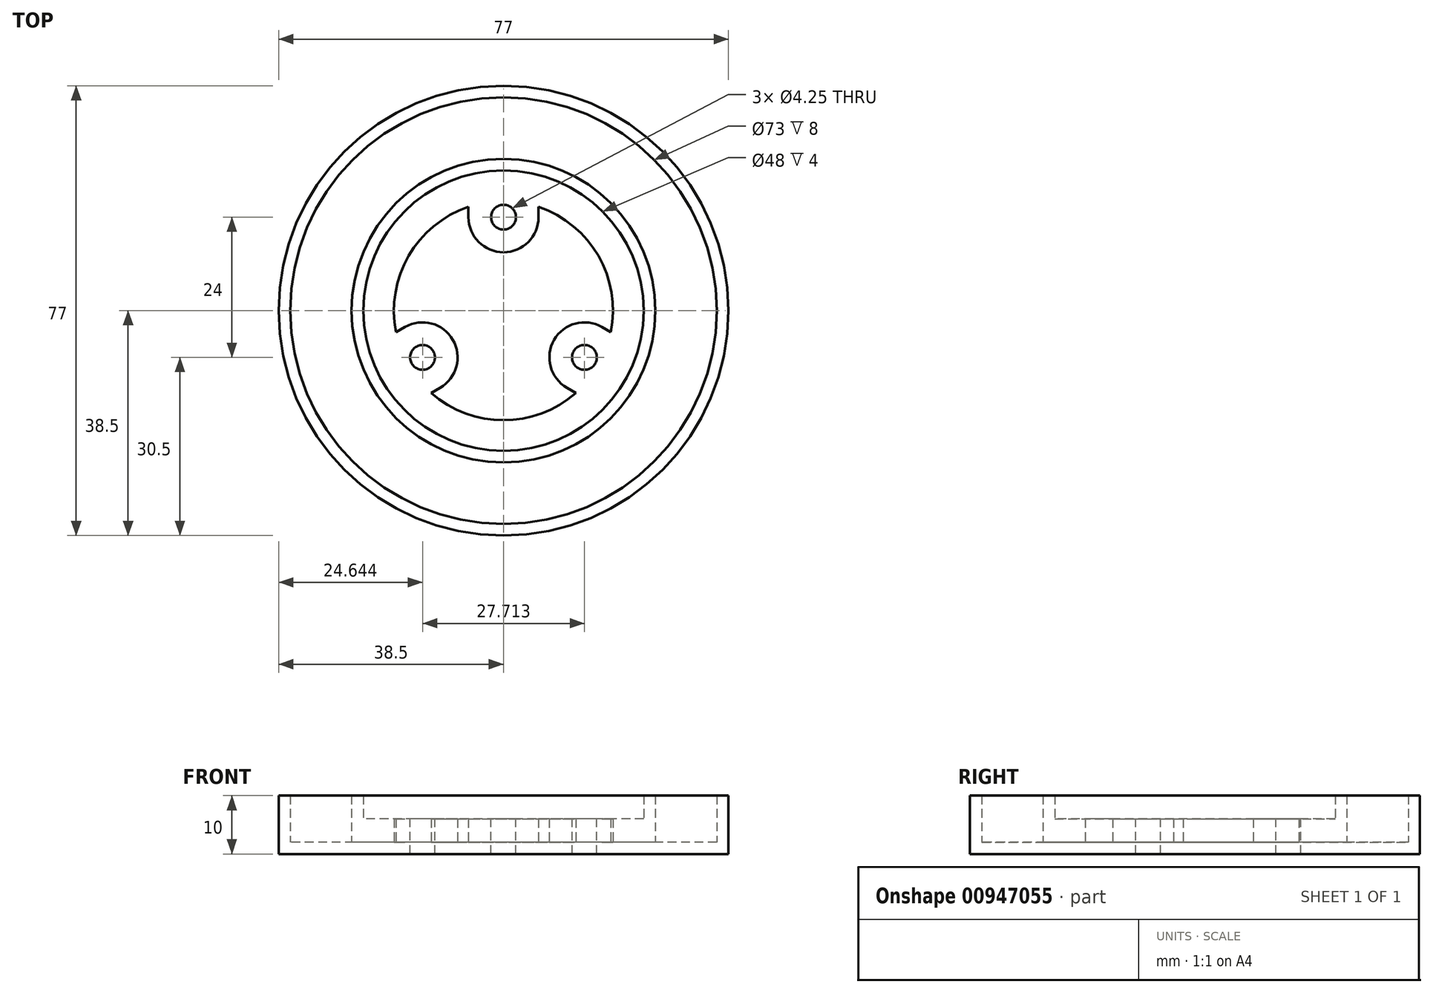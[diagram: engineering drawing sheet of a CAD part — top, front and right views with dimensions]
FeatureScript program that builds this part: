
annotation { "Feature Type Name" : "Feature", "Feature Type Description" : "" }
export const myFeature = defineFeature(function(context is Context, id is Id, definition is map)
    precondition{}
    {
        {
            var Q0;
            Q0=qCreatedBy(makeId("Top.planeOp"),FACE);
            var sketch = newSketch(context, id + "F0", { "sketchPlane" : qUnion([Q0])});
            skCircle(sketch, "E0", {"center": v(0, 0) * mm, "radius": 38.5 * mm});
            skSolve(sketch);
        }
        {
            var Q0;
            Q0=makeQuery(id+"F0.imprint","IMPRINT",FACE,{"disambiguationData":[TD([[makeQuery(id+"F0.imprint","IMPRINT",EDGE,{"derivedFrom":sQuery(id+"F0.wireOp",EDGE,"E0")}),1.0]])]});
            extrude(context, id + "F1", {"entities" : qUnion([Q0]), "depth" : 2 * mm, "offsetDistance" : 25 * mm});
        }
        {
            var Q0;
            Q0=makeQuery(id+"F1.opExtrude","CAP_FACE",FACE,{"disambiguationData":[OSD([sQuery(id+"F0.wireOp",EDGE,"E0")])],"isStart":false});
            var sketch = newSketch(context, id + "F2", { "sketchPlane" : qUnion([Q0])});
            skCircle(sketch, "E1.0", {"center": v(0, 0) * mm, "radius": 38.5 * mm});
            skCircle(sketch, "E2.0", {"center": v(0, 0) * mm, "radius": 36.5 * mm});
            skSolve(sketch);
        }
        {
            var Q0;
            Q0 = qSketchRegion(id + "F2", true);
            extrude(context, id + "F3", {"entities" : qUnion([Q0]), "operationType" : NewBodyOperationType.ADD, "depth" : 8 * mm, "offsetDistance" : 25 * mm});
        }
        {
            var Q0;
            Q0=makeQuery(id+"F1.opExtrude","CAP_FACE",FACE,{"disambiguationData":[OSD([sQuery(id+"F0.wireOp",EDGE,"E0")])],"isStart":false});
            var sketch = newSketch(context, id + "F4", { "sketchPlane" : qUnion([Q0])});
            skCircle(sketch, "E3", {"center": v(0, 0) * mm, "radius": 26 * mm});
            skCircle(sketch, "E4.0", {"center": v(0, 0) * mm, "radius": 24 * mm});
            skSolve(sketch);
        }
        {
            var Q0;
            Q0 = qSketchRegion(id + "F4", true);
            extrude(context, id + "F5", {"entities" : qUnion([Q0]), "operationType" : NewBodyOperationType.ADD, "depth" : 8 * mm, "offsetDistance" : 25 * mm});
        }
        {
            var Q0;
            Q0=makeQuery(id+"F5.boolean.opBoolean","SPLIT",FACE,{"disambiguationData":[TD([makeQuery(id+"F5.opExtrude","SWEPT_FACE",FACE,{"disambiguationData":[OSD([sQuery(id+"F4.wireOp",EDGE,"E4.0")])]})])],"derivedFrom":makeQuery(id+"F1.opExtrude","CAP_FACE",FACE,{"disambiguationData":[OSD([sQuery(id+"F0.wireOp",EDGE,"E0")])],"isStart":false})});
            var sketch = newSketch(context, id + "F6", { "sketchPlane" : qUnion([Q0])});
            skCircle(sketch, "E5", {"center": v(0, 0) * mm, "radius": 18.75 * mm});
            skSolve(sketch);
        }
        {
            var Q0;
            Q0=makeQuery(id+"F6.imprint","IMPRINT",FACE,{"disambiguationData":[TD([[makeQuery(id+"F6.imprint","IMPRINT",EDGE,{"derivedFrom":sQuery(id+"F6.wireOp",EDGE,"E5")}),-1.0]])]});
            extrude(context, id + "F7", {"entities" : qUnion([Q0]), "operationType" : NewBodyOperationType.ADD, "depth" : 4 * mm, "offsetDistance" : 25 * mm});
        }
        {
            var Q0;
            Q0=makeQuery(id+"F5.boolean.opBoolean","SPLIT",FACE,{"disambiguationData":[TD([makeQuery(id+"F5.opExtrude","SWEPT_FACE",FACE,{"disambiguationData":[OSD([sQuery(id+"F4.wireOp",EDGE,"E4.0")])]})])],"derivedFrom":makeQuery(id+"F1.opExtrude","CAP_FACE",FACE,{"disambiguationData":[OSD([sQuery(id+"F0.wireOp",EDGE,"E0")])],"isStart":false})});
            var sketch = newSketch(context, id + "F8", { "sketchPlane" : qUnion([Q0])});
            skCircle(sketch, "E6", {"center": v(0, 0) * mm, "radius": 16 * mm, "construction": true});
            skCircle(sketch, "E7", {"center": v(0, 16) * mm, "radius": 2.12 * mm});
            skCircle(sketch, "E8.1.0", {"center": v(-13.86, -8) * mm, "radius": 2.12 * mm});
            skCircle(sketch, "E8.2.0", {"center": v(13.86, -8) * mm, "radius": 2.12 * mm});
            skSolve(sketch);
        }
        {
            var Q0;
            Q0 = qSketchRegion(id + "F8", true);
            extrude(context, id + "F9", {"entities" : qUnion([Q0]), "operationType" : NewBodyOperationType.REMOVE, "oppositeDirection" : true, "depth" : 25 * mm, "offsetDistance" : 25 * mm, "symmetric" : true});
        }
        {
            var Q0;
            Q0=makeQuery(id+"F5.boolean.opBoolean","SPLIT",FACE,{"disambiguationData":[TD([makeQuery(id+"F5.opExtrude","SWEPT_FACE",FACE,{"disambiguationData":[OSD([sQuery(id+"F4.wireOp",EDGE,"E4.0")])]})])],"derivedFrom":makeQuery(id+"F1.opExtrude","CAP_FACE",FACE,{"disambiguationData":[OSD([sQuery(id+"F0.wireOp",EDGE,"E0")])],"isStart":false})});
            var sketch = newSketch(context, id + "F10", { "sketchPlane" : qUnion([Q0])});
            skCircle(sketch, "E9.0", {"center": v(-13.86, -8) * mm, "radius": 2.12 * mm});
            skCircle(sketch, "E10.0", {"center": v(0, 16) * mm, "radius": 2.12 * mm});
            skCircle(sketch, "E11.0", {"center": v(13.86, -8) * mm, "radius": 2.12 * mm});
            skCircle(sketch, "E12.0", {"center": v(0, 0) * mm, "radius": 18.75 * mm});
            skLineSegment(sketch, "E13", {"start": v(0, 16) * mm, "end": v(-6, 16) * mm, "construction": true});
            skLineSegment(sketch, "E14", {"start": v(0, 16) * mm, "end": v(6, 16) * mm, "construction": true});
            skLineSegment(sketch, "E15", {"start": v(6, 16) * mm, "end": v(6, 17.76) * mm});
            skLineSegment(sketch, "E16", {"start": v(-6, 16) * mm, "end": v(-6, 17.76) * mm});
            skLineSegment(sketch, "E17", {"start": v(0, 16) * mm, "end": v(0, 10) * mm, "construction": true});
            skLineSegment(sketch, "E18", {"start": v(0, 10) * mm, "end": v(-6, 10) * mm});
            skLineSegment(sketch, "E19", {"start": v(-6, 16) * mm, "end": v(-6, 10) * mm});
            skLineSegment(sketch, "E20", {"start": v(6, 16) * mm, "end": v(6, 10) * mm});
            skLineSegment(sketch, "E21", {"start": v(6, 10) * mm, "end": v(0, 10) * mm});
            skLineSegment(sketch, "E22.1.0", {"start": v(-11.66, 0.2) * mm, "end": v(-8.66, -5) * mm});
            skLineSegment(sketch, "E22.1.1", {"start": v(-8.66, -5) * mm, "end": v(-5.66, -10.2) * mm});
            skLineSegment(sketch, "E22.1.2", {"start": v(-10.86, -13.2) * mm, "end": v(-5.66, -10.2) * mm});
            skLineSegment(sketch, "E22.1.3", {"start": v(-10.86, -13.2) * mm, "end": v(-12.38, -14.08) * mm});
            skLineSegment(sketch, "E22.1.4", {"start": v(-16.86, -2.8) * mm, "end": v(-18.38, -3.69) * mm});
            skLineSegment(sketch, "E22.1.5", {"start": v(-16.86, -2.8) * mm, "end": v(-11.66, 0.2) * mm});
            skLineSegment(sketch, "E22.2.0", {"start": v(5.66, -10.2) * mm, "end": v(8.66, -5) * mm});
            skLineSegment(sketch, "E22.2.1", {"start": v(8.66, -5) * mm, "end": v(11.66, 0.2) * mm});
            skLineSegment(sketch, "E22.2.2", {"start": v(16.86, -2.8) * mm, "end": v(11.66, 0.2) * mm});
            skLineSegment(sketch, "E22.2.3", {"start": v(16.86, -2.8) * mm, "end": v(18.38, -3.69) * mm});
            skLineSegment(sketch, "E22.2.4", {"start": v(10.86, -13.2) * mm, "end": v(12.38, -14.08) * mm});
            skLineSegment(sketch, "E22.2.5", {"start": v(10.86, -13.2) * mm, "end": v(5.66, -10.2) * mm});
            skSolve(sketch);
        }
        {
            var Q0;
            {var subQ4=sQuery(id+"F10.wireOp",EDGE,"E15");Q0=makeQuery(id+"F10.imprint","IMPRINT",FACE,{"disambiguationData":[TD([[makeQuery(id+"F10.imprint","IMPRINT",EDGE,{"derivedFrom":subQ4}),1.0]])]});}
            var Q1;
            {var subQ0=sQuery(id+"F10.wireOp",EDGE,"E18");Q1=makeQuery(id+"F10.imprint","IMPRINT",FACE,{"disambiguationData":[TD([[makeQuery(id+"F10.imprint","IMPRINT",EDGE,{"derivedFrom":subQ0}),-1.0]])]});}
            var Q2;
            {var subQ0=sQuery(id+"F10.wireOp",EDGE,"E20");Q2=makeQuery(id+"F10.imprint","IMPRINT",FACE,{"disambiguationData":[TD([[makeQuery(id+"F10.imprint","IMPRINT",EDGE,{"derivedFrom":subQ0}),-1.0]])]});}
            var Q3;
            Q3=makeQuery(id+"F10.imprint","IMPRINT",FACE,{"disambiguationData":[TD([[makeQuery(id+"F10.imprint","IMPRINT",EDGE,{"derivedFrom":sQuery(id+"F10.wireOp",EDGE,"E9.0")}),-1.0]])]});
            var Q4;
            Q4=makeQuery(id+"F10.imprint","IMPRINT",FACE,{"disambiguationData":[TD([[makeQuery(id+"F10.imprint","IMPRINT",EDGE,{"derivedFrom":sQuery(id+"F10.wireOp",EDGE,"E11.0")}),-1.0]])]});
            extrude(context, id + "F11", {"entities" : qUnion([Q0, Q1, Q2, Q3, Q4]), "operationType" : NewBodyOperationType.ADD, "depth" : 4 * mm, "offsetDistance" : 25 * mm});
        }
        {
            var Q0;
            Q0=makeQuery(id+"F11.opExtrude","SWEPT_EDGE",EDGE,{"disambiguationData":[OSD([sQuery(id+"F10.wireOp",EDGE,"E18"),sQuery(id+"F10.wireOp",EDGE,"E19")])]});
            var Q1;
            Q1=makeQuery(id+"F11.opExtrude","SWEPT_EDGE",EDGE,{"disambiguationData":[OSD([sQuery(id+"F10.wireOp",EDGE,"E20"),sQuery(id+"F10.wireOp",EDGE,"E21")])]});
            var Q2;
            Q2=makeQuery(id+"F11.opExtrude","SWEPT_EDGE",EDGE,{"disambiguationData":[OSD([sQuery(id+"F10.wireOp",EDGE,"E22.2.1"),sQuery(id+"F10.wireOp",EDGE,"E22.2.2")])]});
            var Q3;
            Q3=makeQuery(id+"F11.opExtrude","SWEPT_EDGE",EDGE,{"disambiguationData":[OSD([sQuery(id+"F10.wireOp",EDGE,"E22.2.0"),sQuery(id+"F10.wireOp",EDGE,"E22.2.5")])]});
            var Q4;
            Q4=makeQuery(id+"F11.opExtrude","SWEPT_EDGE",EDGE,{"disambiguationData":[OSD([sQuery(id+"F10.wireOp",EDGE,"E22.1.1"),sQuery(id+"F10.wireOp",EDGE,"E22.1.2")])]});
            var Q5;
            Q5=makeQuery(id+"F11.opExtrude","SWEPT_EDGE",EDGE,{"disambiguationData":[OSD([sQuery(id+"F10.wireOp",EDGE,"E22.1.0"),sQuery(id+"F10.wireOp",EDGE,"E22.1.5")])]});
            fillet(context, id + "F12", {"entities" : qUnion([Q0, Q1, Q2, Q3, Q4, Q5]), "tangentPropagation" : true, "radius" : 6 * mm, "defaultsChanged" : true, "vertexSettings" : [], "allowEdgeOverflow" : false});
        }
    });
